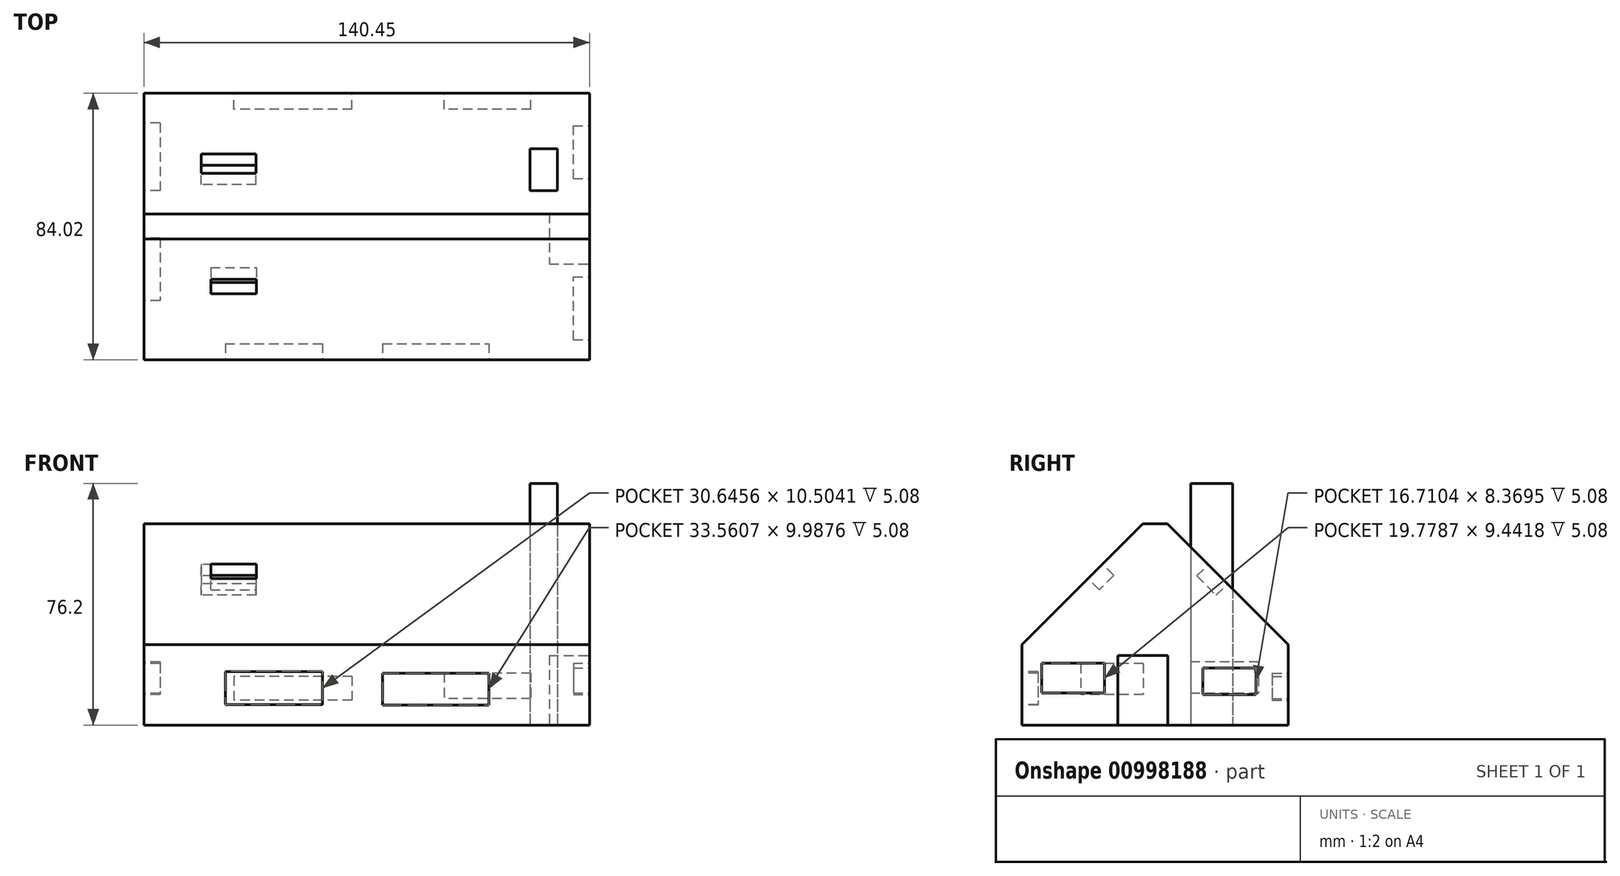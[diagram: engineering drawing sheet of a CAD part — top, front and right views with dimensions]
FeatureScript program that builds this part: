
annotation { "Feature Type Name" : "Feature", "Feature Type Description" : "" }
export const myFeature = defineFeature(function(context is Context, id is Id, definition is map)
    precondition{}
    {
        {
            var Q0;
            Q0=qCreatedBy(makeId("Top.planeOp"),FACE);
            var sketch = newSketch(context, id + "F0", { "sketchPlane" : qUnion([Q0])});
            skLineSegment(sketch, "E0.bottom", {"start": v(0, 30.7) * mm, "end": v(140.45, 30.7) * mm});
            skLineSegment(sketch, "E0.top", {"start": v(0, -53.32) * mm, "end": v(140.45, -53.32) * mm});
            skLineSegment(sketch, "E0.left", {"start": v(0, 30.7) * mm, "end": v(0, -53.32) * mm});
            skLineSegment(sketch, "E0.right", {"start": v(140.45, 30.7) * mm, "end": v(140.45, -53.32) * mm});
            skSolve(sketch);
        }
        {
            var Q0;
            Q0=makeQuery(id+"F0.imprint","IMPRINT",FACE,{"disambiguationData":[TD([[makeQuery(id+"F0.imprint","IMPRINT",EDGE,{"derivedFrom":sQuery(id+"F0.wireOp",EDGE,"E0.bottom")}),-1.0]])]});
            extrude(context, id + "F1", {"entities" : qUnion([Q0]), "depth" : 63.5 * mm, "offsetDistance" : 25.4 * mm});
        }
        {
            var Q0;
            Q0=makeQuery(id+"F1.opExtrude","CAP_EDGE",EDGE,{"disambiguationData":[OSD([sQuery(id+"F0.wireOp",EDGE,"E0.top")])],"isStart":false});
            var Q1;
            Q1=makeQuery(id+"F1.opExtrude","CAP_EDGE",EDGE,{"disambiguationData":[OSD([sQuery(id+"F0.wireOp",EDGE,"E0.bottom")])],"isStart":false});
            chamfer(context, id + "F2", {"entities" : qUnion([Q0, Q1]), "width" : 38.1 * mm, "tangentPropagation" : true});
        }
        {
            var Q0;
            Q0=qCreatedBy(makeId("Top.planeOp"),FACE);
            var sketch = newSketch(context, id + "F3", { "sketchPlane" : qUnion([Q0])});
            skLineSegment(sketch, "E1.bottom", {"start": v(121.7, 13.16) * mm, "end": v(130.36, 13.16) * mm});
            skLineSegment(sketch, "E1.top", {"start": v(121.7, 0) * mm, "end": v(130.36, 0) * mm});
            skLineSegment(sketch, "E1.left", {"start": v(121.7, 13.16) * mm, "end": v(121.7, 0) * mm});
            skLineSegment(sketch, "E1.right", {"start": v(130.36, 13.16) * mm, "end": v(130.36, 0) * mm});
            skSolve(sketch);
        }
        {
            var Q0;
            Q0=makeQuery(id+"F3.imprint","IMPRINT",FACE,{"disambiguationData":[TD([[makeQuery(id+"F3.imprint","IMPRINT",EDGE,{"derivedFrom":sQuery(id+"F3.wireOp",EDGE,"E1.bottom")}),-1.0]])]});
            extrude(context, id + "F4", {"entities" : qUnion([Q0]), "depth" : 76.2 * mm, "offsetDistance" : 25.4 * mm});
        }
        {
            var Q0;
            Q0=makeQuery(id+"F1.opExtrude","SWEPT_FACE",FACE,{"disambiguationData":[OSD([sQuery(id+"F0.wireOp",EDGE,"E0.right")])]});
            var sketch = newSketch(context, id + "F5", { "sketchPlane" : qUnion([Q0])});
            skSolve(sketch);
        }
        {
            var Q0;
            {var subQ0=sQuery(id+"F0.wireOp",EDGE,"E0.right");Q0=makeQuery(id+"F5.imprint","IMPRINT",FACE,{"disambiguationData":[TD([[makeQuery(id+"F5.imprint","IMPRINT",EDGE,{"derivedFrom":makeQuery(id+"F1.opExtrude","CAP_EDGE",EDGE,{"disambiguationData":[OSD([subQ0])],"isStart":true})}),-1.0]])]});}
            var sketch = newSketch(context, id + "F6", { "sketchPlane" : qUnion([Q0])});
            skLineSegment(sketch, "E2.bottom", {"start": v(-7.27, 21.93) * mm, "end": v(-23.06, 21.93) * mm});
            skLineSegment(sketch, "E2.top", {"start": v(-7.27, 0) * mm, "end": v(-23.06, 0) * mm});
            skLineSegment(sketch, "E2.left", {"start": v(-7.27, 21.93) * mm, "end": v(-7.27, 0) * mm});
            skLineSegment(sketch, "E2.right", {"start": v(-23.06, 21.93) * mm, "end": v(-23.06, 0) * mm});
            skSolve(sketch);
        }
        {
            var Q0;
            Q0=makeQuery(id+"F6.imprint","IMPRINT",FACE,{"disambiguationData":[TD([[makeQuery(id+"F6.imprint","IMPRINT",EDGE,{"derivedFrom":sQuery(id+"F6.wireOp",EDGE,"E2.bottom")}),1.0]])]});
            extrude(context, id + "F7", {"entities" : qUnion([Q0]), "operationType" : NewBodyOperationType.REMOVE, "oppositeDirection" : true, "depth" : 12.7 * mm, "offsetDistance" : 25.4 * mm});
        }
        {
            var Q0;
            {var subQ0=sQuery(id+"F0.wireOp",EDGE,"E0.right");Q0=makeQuery(id+"F5.imprint","IMPRINT",FACE,{"disambiguationData":[TD([[makeQuery(id+"F5.imprint","IMPRINT",EDGE,{"derivedFrom":makeQuery(id+"F1.opExtrude","CAP_EDGE",EDGE,{"disambiguationData":[OSD([subQ0])],"isStart":true})}),-1.0]])]});}
            var sketch = newSketch(context, id + "F8", { "sketchPlane" : qUnion([Q0])});
            skSolve(sketch);
        }
        {
            var Q0;
            {var subQ0=sQuery(id+"F0.wireOp",EDGE,"E0.right");Q0=makeQuery(id+"F8.imprint","IMPRINT",FACE,{"disambiguationData":[TD([[makeQuery(id+"F8.imprint","IMPRINT",EDGE,{"derivedFrom":makeQuery(id+"F5.imprint","IMPRINT",EDGE,{"derivedFrom":makeQuery(id+"F1.opExtrude","CAP_EDGE",EDGE,{"disambiguationData":[OSD([subQ0])],"isStart":true})})}),-1.0]])]});}
            var sketch = newSketch(context, id + "F9", { "sketchPlane" : qUnion([Q0])});
            skCircle(sketch, "E3", {"center": v(-10.37, 13.1) * mm, "radius": 0.73 * mm});
            skSolve(sketch);
        }
        {
            var Q0;
            Q0=sQuery(id+"F9.wireOp",EDGE,"E3");
            extrude(context, id + "F10", {"bodyType" : ToolBodyType.SURFACE, "surfaceEntities" : qUnion([Q0]), "depth" : 2.54 * mm, "offsetDistance" : 25.4 * mm});
        }
        {
            var Q0;
            {var subQ0=sQuery(id+"F0.wireOp",EDGE,"E0.right");Q0=makeQuery(id+"F8.imprint","IMPRINT",FACE,{"disambiguationData":[TD([[makeQuery(id+"F8.imprint","IMPRINT",EDGE,{"derivedFrom":makeQuery(id+"F5.imprint","IMPRINT",EDGE,{"derivedFrom":makeQuery(id+"F1.opExtrude","CAP_EDGE",EDGE,{"disambiguationData":[OSD([subQ0])],"isStart":true})})}),-1.0]])]});}
            var sketch = newSketch(context, id + "F11", { "sketchPlane" : qUnion([Q0])});
            skLineSegment(sketch, "E4.bottom", {"start": v(3.77, 17.97) * mm, "end": v(20.48, 17.97) * mm});
            skLineSegment(sketch, "E4.top", {"start": v(3.77, 9.6) * mm, "end": v(20.48, 9.6) * mm});
            skLineSegment(sketch, "E4.left", {"start": v(3.77, 17.97) * mm, "end": v(3.77, 9.6) * mm});
            skLineSegment(sketch, "E4.right", {"start": v(20.48, 17.97) * mm, "end": v(20.48, 9.6) * mm});
            skSolve(sketch);
        }
        {
            var Q0;
            Q0=makeQuery(id+"F11.imprint","IMPRINT",FACE,{"disambiguationData":[TD([[makeQuery(id+"F11.imprint","IMPRINT",EDGE,{"derivedFrom":sQuery(id+"F11.wireOp",EDGE,"E4.bottom")}),-1.0]])]});
            extrude(context, id + "F12", {"entities" : qUnion([Q0]), "operationType" : NewBodyOperationType.REMOVE, "oppositeDirection" : true, "depth" : 5.08 * mm, "offsetDistance" : 25.4 * mm});
        }
        {
            var Q0;
            {var subQ0=sQuery(id+"F0.wireOp",EDGE,"E0.right");Q0=makeQuery(id+"F8.imprint","IMPRINT",FACE,{"disambiguationData":[TD([[makeQuery(id+"F8.imprint","IMPRINT",EDGE,{"derivedFrom":makeQuery(id+"F5.imprint","IMPRINT",EDGE,{"derivedFrom":makeQuery(id+"F1.opExtrude","CAP_EDGE",EDGE,{"disambiguationData":[OSD([subQ0])],"isStart":true})})}),-1.0]])]});}
            var sketch = newSketch(context, id + "F13", { "sketchPlane" : qUnion([Q0])});
            skLineSegment(sketch, "E5.bottom", {"start": v(-47.03, 19.54) * mm, "end": v(-27.25, 19.54) * mm});
            skLineSegment(sketch, "E5.top", {"start": v(-47.03, 10.1) * mm, "end": v(-27.25, 10.1) * mm});
            skLineSegment(sketch, "E5.left", {"start": v(-47.03, 19.54) * mm, "end": v(-47.03, 10.1) * mm});
            skLineSegment(sketch, "E5.right", {"start": v(-27.25, 19.54) * mm, "end": v(-27.25, 10.1) * mm});
            skSolve(sketch);
        }
        {
            var Q0;
            Q0=makeQuery(id+"F13.imprint","IMPRINT",FACE,{"disambiguationData":[TD([[makeQuery(id+"F13.imprint","IMPRINT",EDGE,{"derivedFrom":sQuery(id+"F13.wireOp",EDGE,"E5.bottom")}),-1.0]])]});
            extrude(context, id + "F14", {"entities" : qUnion([Q0]), "operationType" : NewBodyOperationType.REMOVE, "oppositeDirection" : true, "depth" : 5.08 * mm, "offsetDistance" : 25.4 * mm});
        }
        {
            var Q0;
            Q0=makeQuery(id+"F1.opExtrude","SWEPT_FACE",FACE,{"disambiguationData":[OSD([sQuery(id+"F0.wireOp",EDGE,"E0.top")])]});
            var sketch = newSketch(context, id + "F15", { "sketchPlane" : qUnion([Q0])});
            skLineSegment(sketch, "E6.bottom", {"start": v(25.64, 16.94) * mm, "end": v(56.29, 16.94) * mm});
            skLineSegment(sketch, "E6.top", {"start": v(25.64, 6.43) * mm, "end": v(56.29, 6.43) * mm});
            skLineSegment(sketch, "E6.left", {"start": v(25.64, 16.94) * mm, "end": v(25.64, 6.43) * mm});
            skLineSegment(sketch, "E6.right", {"start": v(56.29, 16.94) * mm, "end": v(56.29, 6.43) * mm});
            skSolve(sketch);
        }
        {
            var Q0;
            Q0=makeQuery(id+"F15.imprint","IMPRINT",FACE,{"disambiguationData":[TD([[makeQuery(id+"F15.imprint","IMPRINT",EDGE,{"derivedFrom":sQuery(id+"F15.wireOp",EDGE,"E6.bottom")}),-1.0]])]});
            extrude(context, id + "F16", {"entities" : qUnion([Q0]), "operationType" : NewBodyOperationType.REMOVE, "oppositeDirection" : true, "depth" : 5.08 * mm, "offsetDistance" : 25.4 * mm});
        }
        {
            var Q0;
            Q0=makeQuery(id+"F1.opExtrude","SWEPT_FACE",FACE,{"disambiguationData":[OSD([sQuery(id+"F0.wireOp",EDGE,"E0.top")])]});
            var sketch = newSketch(context, id + "F17", { "sketchPlane" : qUnion([Q0])});
            skLineSegment(sketch, "E7.bottom", {"start": v(75.21, 16.38) * mm, "end": v(108.77, 16.38) * mm});
            skLineSegment(sketch, "E7.top", {"start": v(75.21, 6.4) * mm, "end": v(108.77, 6.4) * mm});
            skLineSegment(sketch, "E7.left", {"start": v(75.21, 16.38) * mm, "end": v(75.21, 6.4) * mm});
            skLineSegment(sketch, "E7.right", {"start": v(108.77, 16.38) * mm, "end": v(108.77, 6.4) * mm});
            skSolve(sketch);
        }
        {
            var Q0;
            Q0=makeQuery(id+"F17.imprint","IMPRINT",FACE,{"disambiguationData":[TD([[makeQuery(id+"F17.imprint","IMPRINT",EDGE,{"derivedFrom":sQuery(id+"F17.wireOp",EDGE,"E7.bottom")}),-1.0]])]});
            extrude(context, id + "F18", {"entities" : qUnion([Q0]), "operationType" : NewBodyOperationType.REMOVE, "oppositeDirection" : true, "depth" : 5.08 * mm, "offsetDistance" : 25.4 * mm});
        }
        {
            var Q0;
            Q0=makeQuery(id+"F1.opExtrude","SWEPT_FACE",FACE,{"disambiguationData":[OSD([sQuery(id+"F0.wireOp",EDGE,"E0.left")])]});
            var sketch = newSketch(context, id + "F19", { "sketchPlane" : qUnion([Q0])});
            skLineSegment(sketch, "E8.bottom", {"start": v(-21.3, 19.88) * mm, "end": v(0, 19.88) * mm});
            skLineSegment(sketch, "E8.top", {"start": v(-21.3, 10.08) * mm, "end": v(0, 10.08) * mm});
            skLineSegment(sketch, "E8.left", {"start": v(-21.3, 19.88) * mm, "end": v(-21.3, 10.08) * mm});
            skLineSegment(sketch, "E8.right", {"start": v(0, 19.88) * mm, "end": v(0, 10.08) * mm});
            skSolve(sketch);
        }
        {
            var Q0;
            Q0=makeQuery(id+"F19.imprint","IMPRINT",FACE,{"disambiguationData":[TD([[makeQuery(id+"F19.imprint","IMPRINT",EDGE,{"derivedFrom":sQuery(id+"F19.wireOp",EDGE,"E8.bottom")}),-1.0]])]});
            extrude(context, id + "F20", {"entities" : qUnion([Q0]), "operationType" : NewBodyOperationType.REMOVE, "oppositeDirection" : true, "depth" : 5.08 * mm, "offsetDistance" : 25.4 * mm});
        }
        {
            var Q0;
            Q0=makeQuery(id+"F1.opExtrude","SWEPT_FACE",FACE,{"disambiguationData":[OSD([sQuery(id+"F0.wireOp",EDGE,"E0.left")])]});
            var sketch = newSketch(context, id + "F21", { "sketchPlane" : qUnion([Q0])});
            skLineSegment(sketch, "E9.bottom", {"start": v(15.02, 19.38) * mm, "end": v(34.72, 19.38) * mm});
            skLineSegment(sketch, "E9.top", {"start": v(15.02, 9.64) * mm, "end": v(34.72, 9.64) * mm});
            skLineSegment(sketch, "E9.left", {"start": v(15.02, 19.38) * mm, "end": v(15.02, 9.64) * mm});
            skLineSegment(sketch, "E9.right", {"start": v(34.72, 19.38) * mm, "end": v(34.72, 9.64) * mm});
            skSolve(sketch);
        }
        {
            var Q0;
            Q0=makeQuery(id+"F21.imprint","IMPRINT",FACE,{"disambiguationData":[TD([[makeQuery(id+"F21.imprint","IMPRINT",EDGE,{"derivedFrom":sQuery(id+"F21.wireOp",EDGE,"E9.bottom")}),-1.0]])]});
            extrude(context, id + "F22", {"entities" : qUnion([Q0]), "operationType" : NewBodyOperationType.REMOVE, "oppositeDirection" : true, "depth" : 5.08 * mm, "offsetDistance" : 25.4 * mm});
        }
        {
            var Q0;
            Q0=makeQuery(id+"F1.opExtrude","SWEPT_FACE",FACE,{"disambiguationData":[OSD([sQuery(id+"F0.wireOp",EDGE,"E0.bottom")])]});
            var sketch = newSketch(context, id + "F23", { "sketchPlane" : qUnion([Q0])});
            skLineSegment(sketch, "E10.bottom", {"start": v(-121.96, 16.4) * mm, "end": v(-94.68, 16.4) * mm});
            skLineSegment(sketch, "E10.top", {"start": v(-121.96, 8.4) * mm, "end": v(-94.68, 8.4) * mm});
            skLineSegment(sketch, "E10.left", {"start": v(-121.96, 16.4) * mm, "end": v(-121.96, 8.4) * mm});
            skLineSegment(sketch, "E10.right", {"start": v(-94.68, 16.4) * mm, "end": v(-94.68, 8.4) * mm});
            skSolve(sketch);
        }
        {
            var Q0;
            Q0=makeQuery(id+"F23.imprint","IMPRINT",FACE,{"disambiguationData":[TD([[makeQuery(id+"F23.imprint","IMPRINT",EDGE,{"derivedFrom":sQuery(id+"F23.wireOp",EDGE,"E10.bottom")}),-1.0]])]});
            extrude(context, id + "F24", {"entities" : qUnion([Q0]), "operationType" : NewBodyOperationType.REMOVE, "oppositeDirection" : true, "depth" : 5.08 * mm, "offsetDistance" : 25.4 * mm});
        }
        {
            var Q0;
            Q0=makeQuery(id+"F1.opExtrude","SWEPT_FACE",FACE,{"disambiguationData":[OSD([sQuery(id+"F0.wireOp",EDGE,"E0.bottom")])]});
            var sketch = newSketch(context, id + "F25", { "sketchPlane" : qUnion([Q0])});
            skLineSegment(sketch, "E11.bottom", {"start": v(-65.56, 15.4) * mm, "end": v(-28.38, 15.4) * mm});
            skLineSegment(sketch, "E11.top", {"start": v(-65.56, 7.9) * mm, "end": v(-28.38, 7.9) * mm});
            skLineSegment(sketch, "E11.left", {"start": v(-65.56, 15.4) * mm, "end": v(-65.56, 7.9) * mm});
            skLineSegment(sketch, "E11.right", {"start": v(-28.38, 15.4) * mm, "end": v(-28.38, 7.9) * mm});
            skSolve(sketch);
        }
        {
            var Q0;
            Q0=makeQuery(id+"F25.imprint","IMPRINT",FACE,{"disambiguationData":[TD([[makeQuery(id+"F25.imprint","IMPRINT",EDGE,{"derivedFrom":sQuery(id+"F25.wireOp",EDGE,"E11.bottom")}),-1.0]])]});
            extrude(context, id + "F26", {"entities" : qUnion([Q0]), "operationType" : NewBodyOperationType.REMOVE, "oppositeDirection" : true, "depth" : 5.08 * mm, "offsetDistance" : 25.4 * mm});
        }
        {
            var Q0;
            Q0=makeQuery(id+"F2.opChamfer","BLEND_FACE",FACE,{"disambiguationData":[OSD([sQuery(id+"F0.wireOp",EDGE,"E0.top")])]});
            var sketch = newSketch(context, id + "F27", { "sketchPlane" : qUnion([Q0])});
            skLineSegment(sketch, "E12.bottom", {"start": v(21.04, 16.22) * mm, "end": v(35.48, 16.22) * mm});
            skLineSegment(sketch, "E12.top", {"start": v(21.04, 9.7) * mm, "end": v(35.48, 9.7) * mm});
            skLineSegment(sketch, "E12.left", {"start": v(21.04, 16.22) * mm, "end": v(21.04, 9.7) * mm});
            skLineSegment(sketch, "E12.right", {"start": v(35.48, 16.22) * mm, "end": v(35.48, 9.7) * mm});
            skSolve(sketch);
        }
        {
            var Q0;
            Q0=makeQuery(id+"F27.imprint","IMPRINT",FACE,{"disambiguationData":[TD([[makeQuery(id+"F27.imprint","IMPRINT",EDGE,{"derivedFrom":sQuery(id+"F27.wireOp",EDGE,"E12.bottom")}),-1.0]])]});
            extrude(context, id + "F28", {"entities" : qUnion([Q0]), "operationType" : NewBodyOperationType.REMOVE, "oppositeDirection" : true, "depth" : 5.08 * mm, "offsetDistance" : 25.4 * mm});
        }
        {
            var Q0;
            Q0=makeQuery(id+"F2.opChamfer","BLEND_FACE",FACE,{"disambiguationData":[OSD([sQuery(id+"F0.wireOp",EDGE,"E0.bottom")])]});
            var sketch = newSketch(context, id + "F29", { "sketchPlane" : qUnion([Q0])});
            skLineSegment(sketch, "E13.bottom", {"start": v(-35.34, 31.95) * mm, "end": v(-18, 31.95) * mm});
            skLineSegment(sketch, "E13.top", {"start": v(-35.34, 23.31) * mm, "end": v(-18, 23.31) * mm});
            skLineSegment(sketch, "E13.left", {"start": v(-35.34, 31.95) * mm, "end": v(-35.34, 23.31) * mm});
            skLineSegment(sketch, "E13.right", {"start": v(-18, 31.95) * mm, "end": v(-18, 23.31) * mm});
            skSolve(sketch);
        }
        {
            var Q0;
            Q0=makeQuery(id+"F29.imprint","IMPRINT",FACE,{"disambiguationData":[TD([[makeQuery(id+"F29.imprint","IMPRINT",EDGE,{"derivedFrom":sQuery(id+"F29.wireOp",EDGE,"E13.bottom")}),-1.0]])]});
            extrude(context, id + "F30", {"entities" : qUnion([Q0]), "operationType" : NewBodyOperationType.REMOVE, "oppositeDirection" : true, "depth" : 5.08 * mm, "offsetDistance" : 25.4 * mm});
        }
    });
